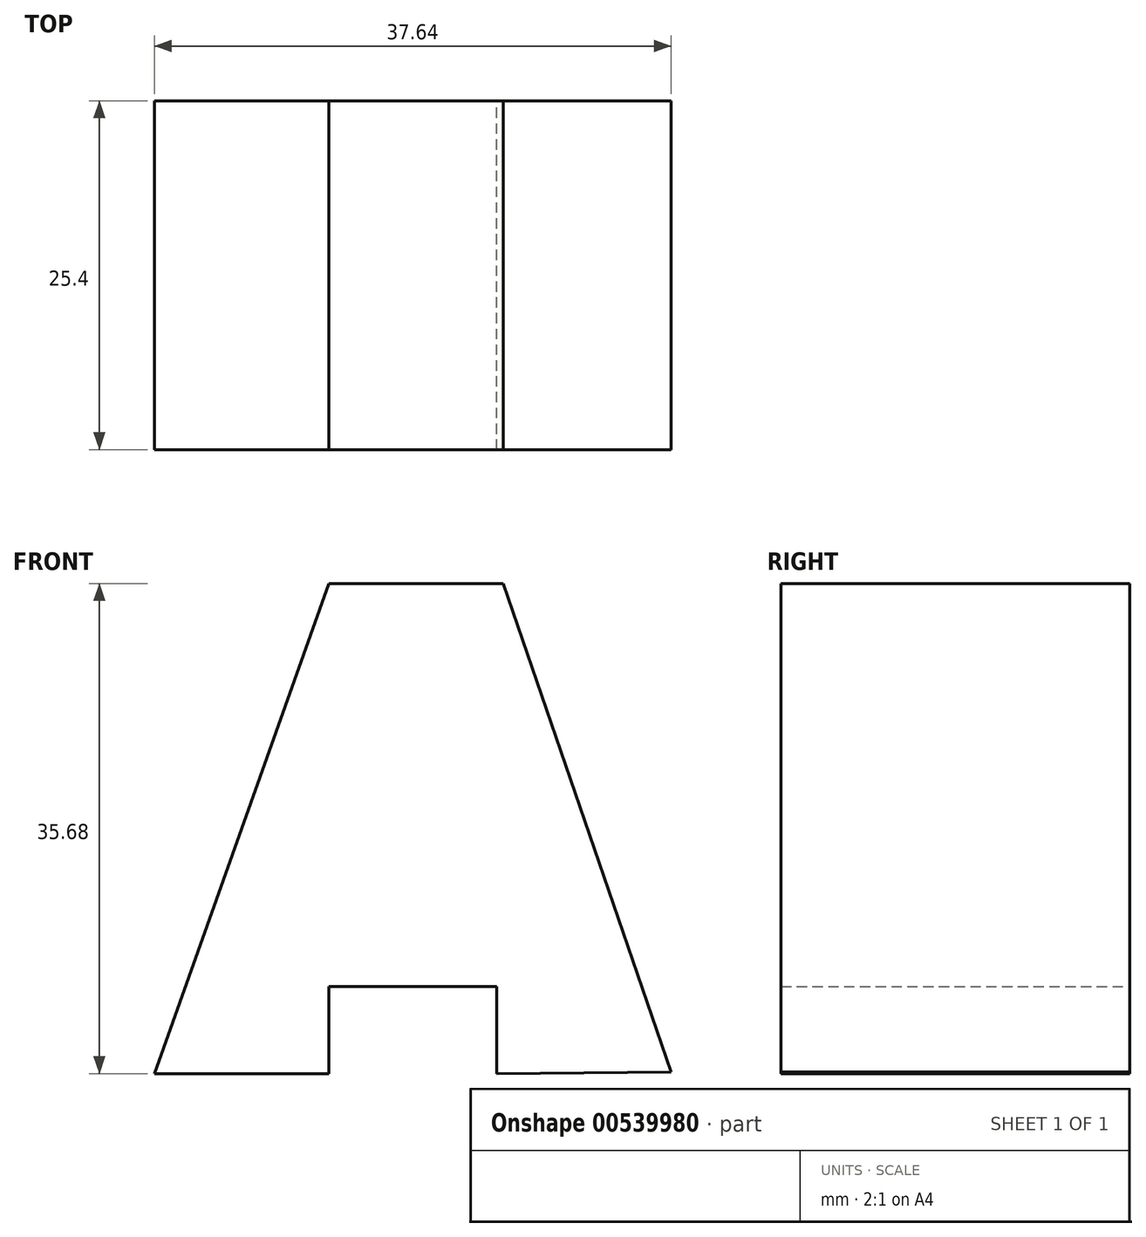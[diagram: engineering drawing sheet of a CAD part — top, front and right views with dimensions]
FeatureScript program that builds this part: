
annotation { "Feature Type Name" : "Feature", "Feature Type Description" : "" }
export const myFeature = defineFeature(function(context is Context, id is Id, definition is map)
    precondition{}
    {
        {
            var Q0;
            Q0=qCreatedBy(makeId("Front.planeOp"),FACE);
            var sketch = newSketch(context, id + "F0", { "sketchPlane" : qUnion([Q0])});
            skLineSegment(sketch, "E0", {"start": v(-6.45, 29.33) * mm, "end": v(6.25, 29.33) * mm});
            skLineSegment(sketch, "E1", {"start": v(6.25, 29.33) * mm, "end": v(18.5, -6.23) * mm});
            skLineSegment(sketch, "E2", {"start": v(-6.45, 29.33) * mm, "end": v(-19.15, -6.35) * mm});
            skLineSegment(sketch, "E3", {"start": v(-19.15, -6.35) * mm, "end": v(-6.45, -6.35) * mm});
            skLineSegment(sketch, "E4", {"start": v(-6.45, -6.35) * mm, "end": v(-6.45, 0) * mm});
            skLineSegment(sketch, "E5", {"start": v(-6.45, 0) * mm, "end": v(6.25, 0) * mm});
            skLineSegment(sketch, "E6", {"start": v(5.8, 0) * mm, "end": v(5.8, -6.35) * mm});
            skLineSegment(sketch, "E7", {"start": v(5.8, -6.35) * mm, "end": v(18.5, -6.23) * mm});
            skSolve(sketch);
        }
        {
            var Q0;
            Q0 = qSketchRegion(id + "F0", true);
            extrude(context, id + "F1", {"entities" : qUnion([Q0]), "depth" : 25.4 * mm, "offsetDistance" : 25.4 * mm});
        }
    });
